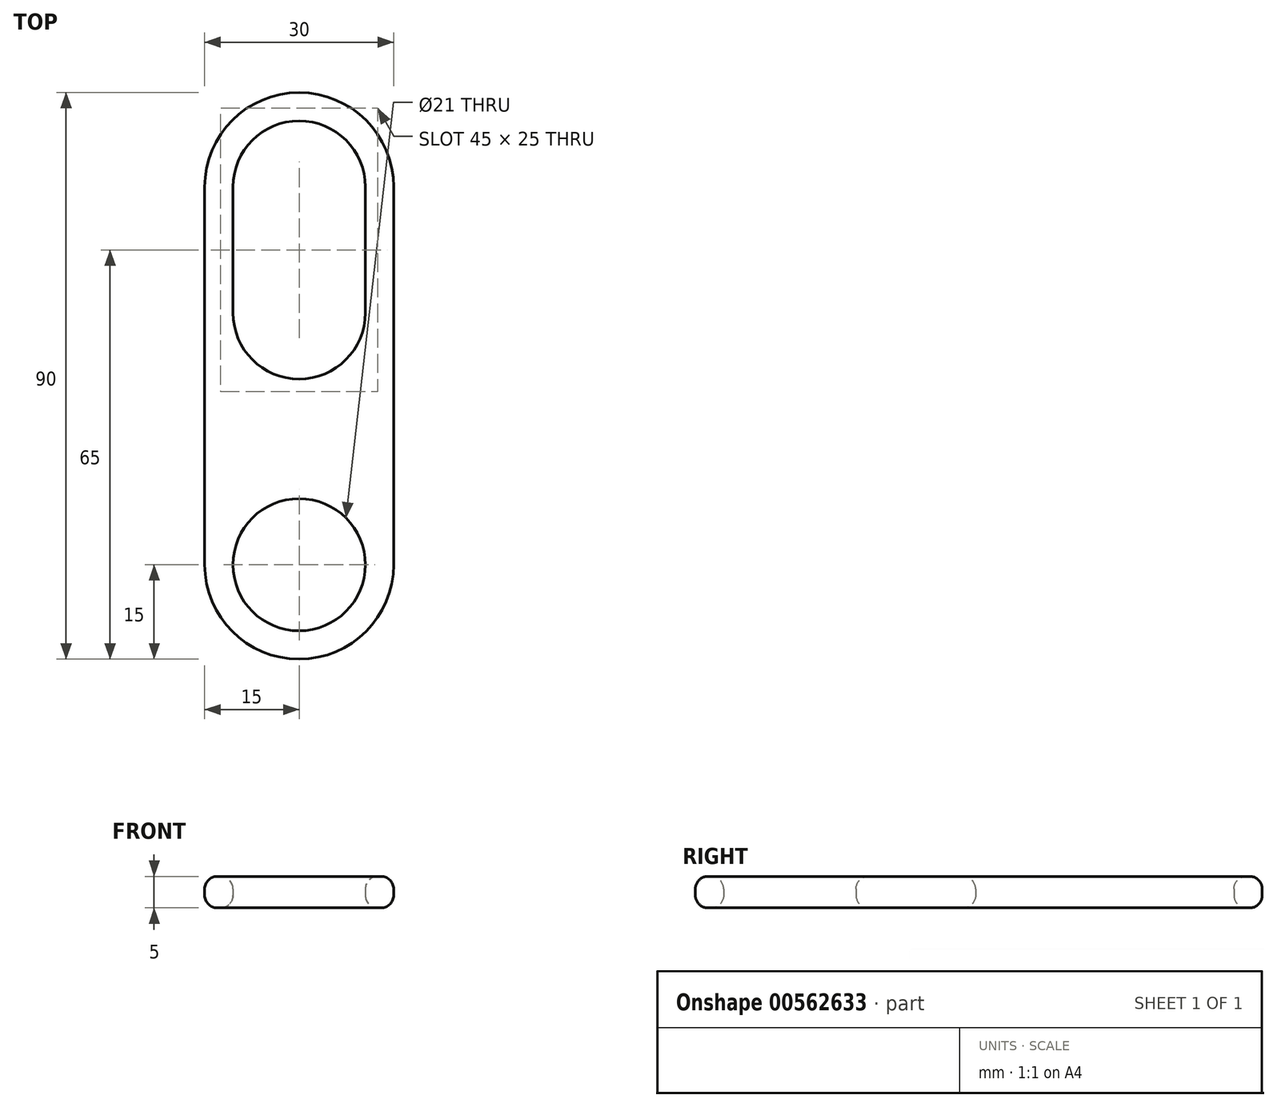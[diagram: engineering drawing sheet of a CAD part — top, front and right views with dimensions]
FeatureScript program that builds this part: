
annotation { "Feature Type Name" : "Feature", "Feature Type Description" : "" }
export const myFeature = defineFeature(function(context is Context, id is Id, definition is map)
    precondition{}
    {
        {
            var Q0;
            Q0=qCreatedBy(makeId("Top.planeOp"),FACE);
            var sketch = newSketch(context, id + "F0", { "sketchPlane" : qUnion([Q0])});
            skLineSegment(sketch, "E0", {"start": v(0, 30) * mm, "end": v(0, -30) * mm});
            skArc(sketch, "E1.0.startCap", {"start": v(-15, 30) * mm, "mid": v(0, 45) * mm, "end": v(15, 30) * mm});
            skArc(sketch, "E1.0.endCap", {"start": v(15, -30) * mm, "mid": v(0, -45) * mm, "end": v(-15, -30) * mm});
            skLineSegment(sketch, "E1.0.left", {"start": v(15, 30) * mm, "end": v(15, -30) * mm});
            skLineSegment(sketch, "E1.0.right", {"start": v(-15, 30) * mm, "end": v(-15, -30) * mm});
            skArc(sketch, "E2", {"start": v(10.5, 30) * mm, "mid": v(0, 40.5) * mm, "end": v(-10.5, 30) * mm});
            skPoint(sketch, "E3.center", {"position": v(0, -0.5) * mm});
            skArc(sketch, "E4", {"start": v(-10.5, 10) * mm, "mid": v(0, -0.5) * mm, "end": v(10.5, 10) * mm});
            skLineSegment(sketch, "E5", {"start": v(10.5, 30) * mm, "end": v(10.5, 10) * mm});
            skLineSegment(sketch, "E6", {"start": v(-10.5, 30) * mm, "end": v(-10.5, 10) * mm});
            skPoint(sketch, "E7.orphan", {"position": v(-12.33, 0) * mm});
            skPoint(sketch, "E8.end.orphan", {"position": v(15, 0) * mm});
            skCircle(sketch, "E9", {"center": v(0, -30) * mm, "radius": 10.5 * mm});
            skSolve(sketch);
        }
        {
            var Q0;
            Q0=qSketchRegion(id+"F0",true);
            extrude(context, id + "F1", {"entities" : qUnion([Q0]), "depth" : 5 * mm, "offsetDistance" : 25 * mm});
        }
        {
            var Q0;
            Q0=makeQuery(id+"F1.opExtrude","CAP_EDGE",EDGE,{"disambiguationData":[OSD([sQuery(id+"F0.wireOp",EDGE,"E2")])],"isStart":false});
            var Q1;
            Q1=makeQuery(id+"F1.opExtrude","CAP_EDGE",EDGE,{"disambiguationData":[OSD([sQuery(id+"F0.wireOp",EDGE,"E2")])],"isStart":true});
            var Q2;
            Q2=makeQuery(id+"F1.opExtrude","CAP_EDGE",EDGE,{"disambiguationData":[OSD([sQuery(id+"F0.wireOp",EDGE,"E1.0.left")])],"isStart":true});
            var Q3;
            Q3=makeQuery(id+"F1.opExtrude","CAP_EDGE",EDGE,{"disambiguationData":[OSD([sQuery(id+"F0.wireOp",EDGE,"E9")])],"isStart":false});
            var Q4;
            Q4=makeQuery(id+"F1.opExtrude","CAP_EDGE",EDGE,{"disambiguationData":[OSD([sQuery(id+"F0.wireOp",EDGE,"E9")])],"isStart":true});
            fillet(context, id + "F2", {"entities" : qUnion([Q0, Q1, Q2, Q3, Q4]), "radius" : 2 * mm, "tangentPropagation" : true, "allowEdgeOverflow" : false});
        }
        {
            var Q0;
            Q0=makeQuery(id+"F1.opExtrude","CAP_EDGE",EDGE,{"disambiguationData":[OSD([sQuery(id+"F0.wireOp",EDGE,"E1.0.right")])],"isStart":false});
            fillet(context, id + "F3", {"entities" : qUnion([Q0]), "radius" : 2 * mm, "tangentPropagation" : true, "allowEdgeOverflow" : false});
        }
    });
